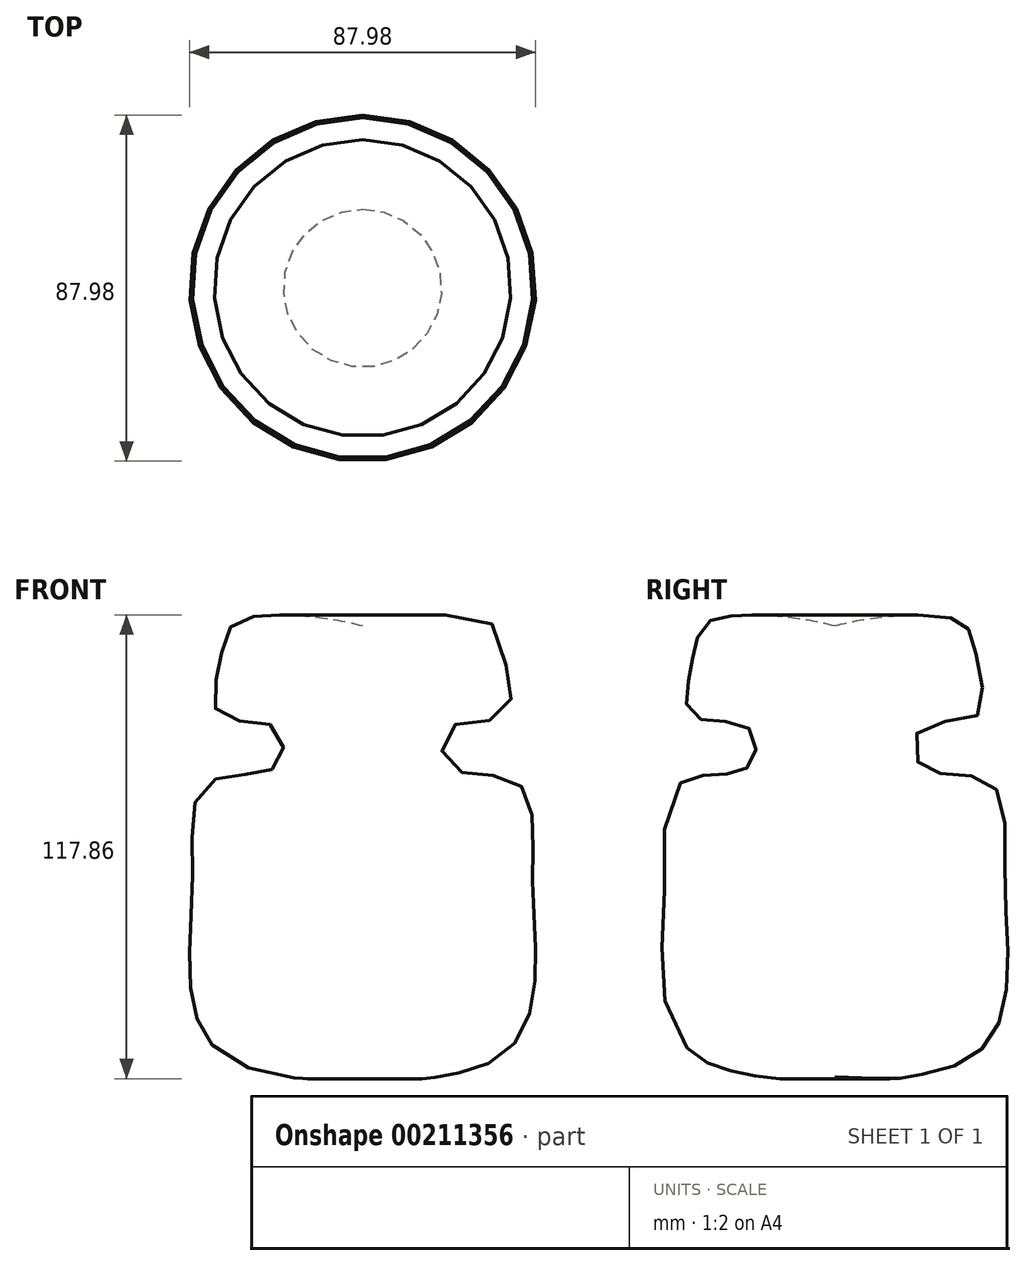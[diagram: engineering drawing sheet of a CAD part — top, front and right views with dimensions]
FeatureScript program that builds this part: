
annotation { "Feature Type Name" : "Feature", "Feature Type Description" : "" }
export const myFeature = defineFeature(function(context is Context, id is Id, definition is map)
    precondition{}
    {
        {
            var Q0;
            Q0=qCreatedBy(makeId("Right.planeOp"),FACE);
            var sketch = newSketch(context, id + "F0", { "sketchPlane" : qUnion([Q0])});
            skLineSegment(sketch, "E0", {"start": v(0, 57.2) * mm, "end": v(0, -52.97) * mm});
            skSolve(sketch);
        }
        {
            var Q0;
            Q0=qCreatedBy(makeId("Right.planeOp"),FACE);
            var sketch = newSketch(context, id + "F1", { "sketchPlane" : qUnion([Q0])});
            skLineSegment(sketch, "E1", {"start": v(0, 58.22) * mm, "end": v(0, -53.58) * mm});
            skSolve(sketch);
        }
        {
            var Q0;
            Q0=qCreatedBy(makeId("Right.planeOp"),FACE);
            var sketch = newSketch(context, id + "F2", { "sketchPlane" : qUnion([Q0])});
            skFitSpline(sketch, "E2", {"points": [v(-17.35, 36.02) * mm, v(5.65, 51.56) * mm, v(40.36, 42.48) * mm, v(49.64, 33) * mm, v(43.38, 25.73) * mm, v(42.98, 14.43) * mm, v(42.58, 8.78) * mm, v(47.02, -1.92) * mm, v(39.95, -15.84) * mm, v(34.1, -31.38) * mm, v(31.08, -49.54) * mm, v(-11.5, -50.35) * mm, v(-24.21, -45.3) * mm, v(-24.01, -45.3) * mm], "startDerivative": vector(193, 199.9) * mm, "endDerivative": vector(31.13, -4.16) * mm});
            skLineSegment(sketch, "E3", {"start": v(0, 54.58) * mm, "end": v(0, -55.6) * mm});
            skSolve(sketch);
        }
        {
            var Q0;
            {var subQ0=sQuery(id+"F2.wireOp",EDGE,"E3");var subQ1=sQuery(id+"F2.wireOp",EDGE,"E2");var subQ2=makeQuery(id+"F2.imprint","INTERSECT",VERTEX,{"disambiguationData":[OD(0.0)],"derivedFrom":[subQ1,subQ0]});Q0=makeQuery(id+"F2.imprint","IMPRINT",FACE,{"disambiguationData":[TD([[makeQuery(id+"F2.imprint","IMPRINT",EDGE,{"disambiguationData":[TD([[subQ2,1.0]])],"derivedFrom":subQ1}),-1.0]])]});}
            var Q1;
            Q1=sQuery(id+"F2.wireOp",EDGE,"E3");
            revolve(context, id + "F3", {"entities" : qUnion([Q0]), "axis" : qUnion([Q1]), "revolveType" : RevolveType.FULL});
        }
        {
            var Q0;
            Q0=makeQuery(id+"F3.opRevolve","SWEPT_BODY",BODY,{"disambiguationData":[OSD([sQuery(id+"F2.wireOp",EDGE,"E2"),sQuery(id+"F2.wireOp",EDGE,"E3")])]});
            deleteBodies(context, id + "F4", {"entities" : qUnion([Q0])});
        }
        {
            var Q0;
            Q0=qCreatedBy(makeId("Right.planeOp"),FACE);
            var sketch = newSketch(context, id + "F5", { "sketchPlane" : qUnion([Q0])});
            skFitSpline(sketch, "E4", {"points": [v(-2.62, 56.8) * mm, v(11.1, 59.63) * mm, v(28.86, 59.63) * mm, v(33.9, 56.6) * mm, v(36.52, 46.92) * mm, v(36.12, 34.6) * mm, v(22, 31.58) * mm, v(21.6, 22.1) * mm, v(31.08, 19.67) * mm, v(41.17, 15.64) * mm, v(43.18, -4.94) * mm, v(44, -27.75) * mm, v(41.37, -44.1) * mm, v(32.7, -53.37) * mm, v(19.78, -57) * mm, v(14.53, -57.61) * mm, v(-4.04, -57.2) * mm, v(-22, -57) * mm, v(-22.6, -56.4) * mm, v(-22.6, -56.6) * mm], "startDerivative": vector(212.9, 55.1) * mm, "endDerivative": vector(3.38, -40.89) * mm});
            skLineSegment(sketch, "E5", {"start": v(0, 62.45) * mm, "end": v(0, -63.87) * mm});
            skSolve(sketch);
        }
        {
            var Q0;
            {var subQ0=sQuery(id+"F5.wireOp",EDGE,"E5");var subQ1=sQuery(id+"F5.wireOp",EDGE,"E4");var subQ2=makeQuery(id+"F5.imprint","INTERSECT",VERTEX,{"disambiguationData":[OD(0.0)],"derivedFrom":[subQ1,subQ0]});Q0=makeQuery(id+"F5.imprint","IMPRINT",FACE,{"disambiguationData":[TD([[makeQuery(id+"F5.imprint","IMPRINT",EDGE,{"disambiguationData":[TD([[subQ2,1.0]])],"derivedFrom":subQ1}),-1.0]])]});}
            var Q1;
            Q1=sQuery(id+"F5.wireOp",EDGE,"E5");
            revolve(context, id + "F6", {"entities" : qUnion([Q0]), "axis" : qUnion([Q1]), "revolveType" : RevolveType.FULL});
        }
    });
